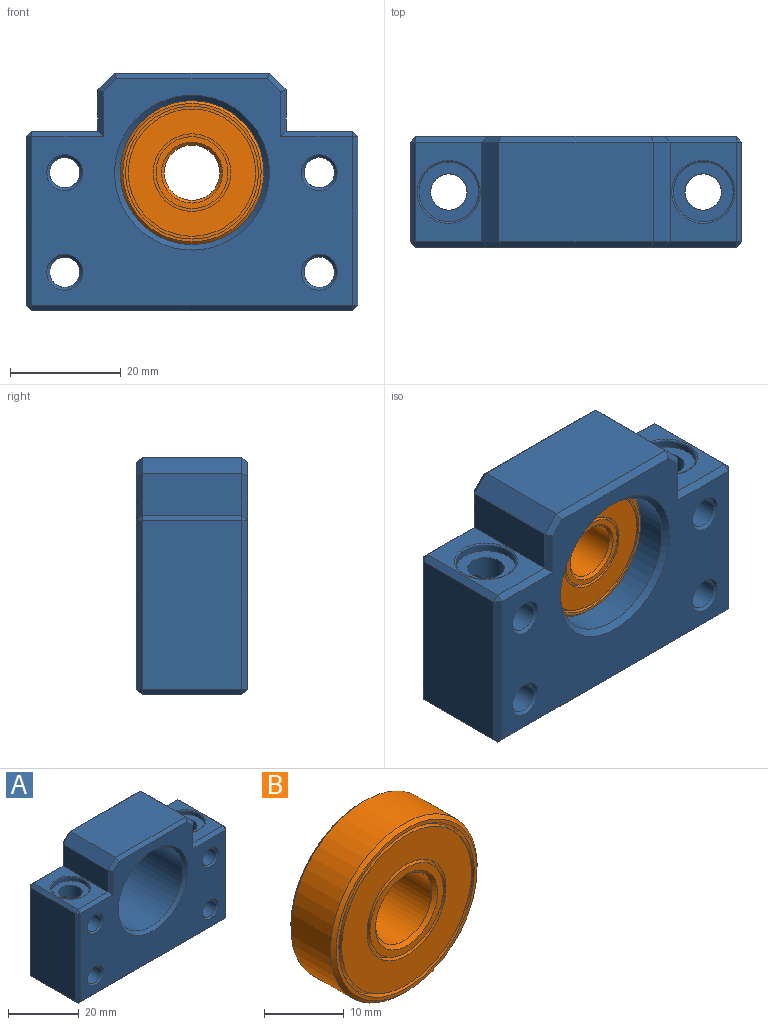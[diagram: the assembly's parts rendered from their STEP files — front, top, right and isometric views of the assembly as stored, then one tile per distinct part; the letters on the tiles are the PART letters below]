
ASSEMBLY  parts=2 mates=1
PART A: 73 faces, bbox 60x20x43 mm
  f0: cylinder r=3.3mm len=30.5mm, axis (0,0,-1), area 525.6mm2, adj f3,f4,f52,f55,f57,f61
  f1: cylinder r=2.75mm len=7.68mm, axis (0,1,0), area 118.9mm2, adj f56,f64
  f2: cylinder r=2.75mm len=7.68mm, axis (0,1,0), area 118.9mm2, adj f56,f63
  f3: cylinder r=2.75mm len=7.68mm, axis (0,1,0), area 119mm2, adj f0,f66
  f4: cylinder r=2.75mm len=7.68mm, axis (0,1,0), area 119mm2, adj f0,f65
  f5: plane 58x41mm, normal (0,-1,0), area 1350.7mm2, adj f18,f20,f21,f22,f23,f24,f27,f28
  f6: plane 58x41mm, normal (0,1,0), area 1350.7mm2, adj f19,f25,f26,f29,f30,f33,f34,f40
  f7: plane 58x18mm, normal (0,0,-1), area 953.3mm2, adj f37,f46,f47,f51,f61,f62
  f8: plane 30.5x18mm, normal (1,0,0), area 549mm2, adj f38,f39,f47,f48
  f9: plane 18x12mm, normal (0,0,1), area 113.9mm2, adj f10,f28,f39,f40,f71
  f10: plane 18x7.5mm, normal (1,0,0), area 135mm2, adj f9,f16,f24,f33
  f11: plane 28x18mm, normal (0,0,1), area 504mm2, adj f16,f17,f20,f25
  f12: plane 18x7.5mm, normal (-1,0,0), area 135mm2, adj f13,f17,f23,f30
  f13: plane 18x12mm, normal (0,0,1), area 113.9mm2, adj f12,f27,f34,f35,f72
  f14: plane 30.5x18mm, normal (-1,0,0), area 549mm2, adj f35,f36,f45,f46
  f15: cylinder r=13mm len=26mm, axis (0,1,0), area 1470.3mm2, adj f18,f19
  f16: plane 18x3mm, normal (0.71,0,0.71), area 76.4mm2, adj f10,f11,f22,f29
  f17: plane 18x3mm, normal (-0.71,0,0.71), area 76.4mm2, adj f11,f12,f21,f26
  f18: cone r=13mm half-angle=45deg, axis (0,-1,0), area 120mm2, adj f5,f15
  f19: cone r=14mm half-angle=45deg, axis (0,1,0), area 120mm2, adj f6,f15
  f20: plane 28x1mm, normal (0,-0.71,0.71), area 39mm2, adj f5,f11,f21,f22
  f21: plane 3.41x3.41mm, normal (-0.5,-0.71,0.5), area 5.4mm2, adj f5,f17,f20,f23
  f22: plane 3.41x3.41mm, normal (0.5,-0.71,0.5), area 5.4mm2, adj f5,f16,f20,f24
  f23: plane 8.5x1mm, normal (-0.71,-0.71,0), area 11mm2, adj f5,f12,f21,f27
  f24: plane 8.5x1mm, normal (0.71,-0.71,0), area 11mm2, adj f5,f10,f22,f28
  f25: plane 28x1mm, normal (0,0.71,0.71), area 39mm2, adj f6,f11,f26,f29
  f26: plane 3.41x3.41mm, normal (-0.5,0.71,0.5), area 5.4mm2, adj f6,f17,f25,f30
  f27: plane 13x1mm, normal (0,-0.71,0.71), area 17.7mm2, adj f5,f13,f23,f31
  f28: plane 13x1mm, normal (0,-0.71,0.71), area 17.7mm2, adj f5,f9,f24,f32
  f29: plane 3.41x3.41mm, normal (0.5,0.71,0.5), area 5.4mm2, adj f6,f16,f25,f33
  f30: plane 8.5x1mm, normal (-0.71,0.71,0), area 11mm2, adj f6,f12,f26,f34
  f31: plane 1x1mm, normal (-0.58,-0.58,0.58), area 0.9mm2, adj f27,f35,f36
  f32: plane 1x1mm, normal (0.58,-0.58,0.58), area 0.9mm2, adj f28,f38,f39
  f33: plane 8.5x1mm, normal (0.71,0.71,0), area 11mm2, adj f6,f10,f29,f40
  f34: plane 13x1mm, normal (0,0.71,0.71), area 17.7mm2, adj f6,f13,f30,f41
  f35: plane 18x1mm, normal (-0.71,0,0.71), area 25.5mm2, adj f13,f14,f31,f41
  f36: plane 30.5x1mm, normal (-0.71,-0.71,0), area 43.1mm2, adj f5,f14,f31,f42
  f37: plane 58x1mm, normal (0,-0.71,-0.71), area 82mm2, adj f5,f7,f42,f43
  f38: plane 30.5x1mm, normal (0.71,-0.71,0), area 43.1mm2, adj f5,f8,f32,f43
  f39: plane 18x1mm, normal (0.71,0,0.71), area 25.5mm2, adj f8,f9,f32,f44
  f40: plane 13x1mm, normal (0,0.71,0.71), area 17.7mm2, adj f6,f9,f33,f44
  f41: plane 1x1mm, normal (-0.58,0.58,0.58), area 0.9mm2, adj f34,f35,f45
  f42: plane 1x1mm, normal (-0.58,-0.58,-0.58), area 0.9mm2, adj f36,f37,f46
  f43: plane 1x1mm, normal (0.58,-0.58,-0.58), area 0.9mm2, adj f37,f38,f47
  f44: plane 1x1mm, normal (0.58,0.58,0.58), area 0.9mm2, adj f39,f40,f48
  f45: plane 30.5x1mm, normal (-0.71,0.71,0), area 43.1mm2, adj f6,f14,f41,f49
  f46: plane 18x1mm, normal (-0.71,0,-0.71), area 25.5mm2, adj f7,f14,f42,f49
  f47: plane 18x1mm, normal (0.71,0,-0.71), area 25.5mm2, adj f7,f8,f43,f50
  f48: plane 30.5x1mm, normal (0.71,0.71,0), area 43.1mm2, adj f6,f8,f44,f50
  f49: plane 1x1mm, normal (-0.58,0.58,-0.58), area 0.9mm2, adj f45,f46,f51
  f50: plane 1x1mm, normal (0.58,0.58,-0.58), area 0.9mm2, adj f47,f48,f51
  f51: plane 58x1mm, normal (0,0.71,-0.71), area 82mm2, adj f6,f7,f49,f50
  f52: cylinder r=2.75mm len=7.68mm, axis (0,1,0), area 119mm2, adj f0,f70
  f53: cylinder r=2.75mm len=7.68mm, axis (0,1,0), area 119mm2, adj f56,f67
  f54: cylinder r=2.75mm len=7.68mm, axis (0,1,0), area 119mm2, adj f56,f68
  f55: cylinder r=2.75mm len=7.68mm, axis (0,1,0), area 119mm2, adj f0,f69
  f56: cylinder r=3.3mm len=30.5mm, axis (0,0,-1), area 525.6mm2, adj f1,f2,f53,f54,f59,f62
  f57: plane 10.8x10.8mm, normal (0,0,1), area 57.4mm2, adj f0,f58
  f58: cylinder r=5.4mm len=10.8mm, axis (0,0,1), area 40.7mm2, adj f57,f71
  f59: plane 10.8x10.8mm, normal (0,0,1), area 57.4mm2, adj f56,f60
  f60: cylinder r=5.4mm len=10.8mm, axis (0,0,1), area 40.7mm2, adj f59,f72
  f61: cone r=3.3mm half-angle=45deg, axis (0,0,-1), area 15.8mm2, adj f0,f7
  f62: cone r=3.3mm half-angle=45deg, axis (0,0,-1), area 15.8mm2, adj f7,f56
  f63: cone r=3.25mm half-angle=45deg, axis (0,-1,0), area 13.3mm2, adj f2,f5
  f64: cone r=3.25mm half-angle=45deg, axis (0,-1,0), area 13.3mm2, adj f1,f5
  f65: cone r=3.25mm half-angle=45deg, axis (0,-1,0), area 13.3mm2, adj f4,f5
  f66: cone r=3.25mm half-angle=45deg, axis (0,-1,0), area 13.3mm2, adj f3,f5
  f67: cone r=2.75mm half-angle=45deg, axis (0,1,0), area 13.3mm2, adj f6,f53
  f68: cone r=2.75mm half-angle=45deg, axis (0,1,0), area 13.3mm2, adj f6,f54
  f69: cone r=2.75mm half-angle=45deg, axis (0,1,0), area 13.3mm2, adj f6,f55
  f70: cone r=2.75mm half-angle=45deg, axis (0,1,0), area 13.3mm2, adj f6,f52
  f71: torus R=5.7mm, axis (0,0,-1), area 16.3mm2, adj f9,f58
  f72: torus R=5.7mm, axis (0,0,-1), area 16.3mm2, adj f13,f60
PART B: 24 faces, bbox 26x8x26 mm
  f0: plane 13x13mm, normal (0,1,0), area 37.7mm2, adj f17,f22
  f1: plane 13x13mm, normal (0,-1,0), area 37.7mm2, adj f10,f21
  f2: cylinder r=5mm len=10mm, axis (0,1,0), area 219.9mm2, adj f21,f22
  f3: cylinder r=13mm len=26mm, axis (0,1,0), area 571.8mm2, adj f20,f23
  f4: plane 25x25mm, normal (0,-1,0), area 38.5mm2, adj f7,f20
  f5: plane 25x25mm, normal (0,1,0), area 38.5mm2, adj f14,f23
  f6: cylinder r=11.5mm len=23mm, axis (0,-1,0), area 72.3mm2, adj f8,f9
  f7: cylinder r=12mm len=24mm, axis (0,-1,0), area 75.4mm2, adj f4,f8
  f8: plane 24x24mm, normal (0,-1,0), area 36.9mm2, adj f6,f7
  f9: plane 23x23mm, normal (0,-1,0), area 261.5mm2, adj f6,f11
  f10: cylinder r=6.5mm len=13mm, axis (0,-1,0), area 40.8mm2, adj f1,f12
  f11: cylinder r=7mm len=14mm, axis (0,-1,0), area 44mm2, adj f9,f12
  f12: plane 14x14mm, normal (0,-1,0), area 21.2mm2, adj f10,f11
  f13: cylinder r=11.5mm len=23mm, axis (0,1,0), area 72.3mm2, adj f15,f16
  f14: cylinder r=12mm len=24mm, axis (0,1,0), area 75.4mm2, adj f5,f15
  f15: plane 24x24mm, normal (0,1,0), area 36.9mm2, adj f13,f14
  f16: plane 23x23mm, normal (0,1,0), area 261.5mm2, adj f13,f18
  f17: cylinder r=6.5mm len=13mm, axis (0,1,0), area 40.8mm2, adj f0,f19
  f18: cylinder r=7mm len=14mm, axis (0,1,0), area 44mm2, adj f16,f19
  f19: plane 14x14mm, normal (0,1,0), area 21.2mm2, adj f17,f18
  f20: cone r=12.5mm half-angle=45deg, axis (0,1,0), area 56.6mm2, adj f3,f4
  f21: cone r=5mm half-angle=45deg, axis (0,-1,0), area 23.3mm2, adj f1,f2
  f22: cone r=5.5mm half-angle=45deg, axis (0,1,0), area 23.3mm2, adj f0,f2
  f23: cone r=13mm half-angle=45deg, axis (0,-1,0), area 56.6mm2, adj f3,f5
PLACE A t=(-7.54,2.77,17.19)mm fixed
PLACE B t=(-7.54,-3.23,-0.81)mm
MATE revolute B.f2 <-> A.f15  axis (0,1,0) through (-7.54,-7.23,-0.81)mm
